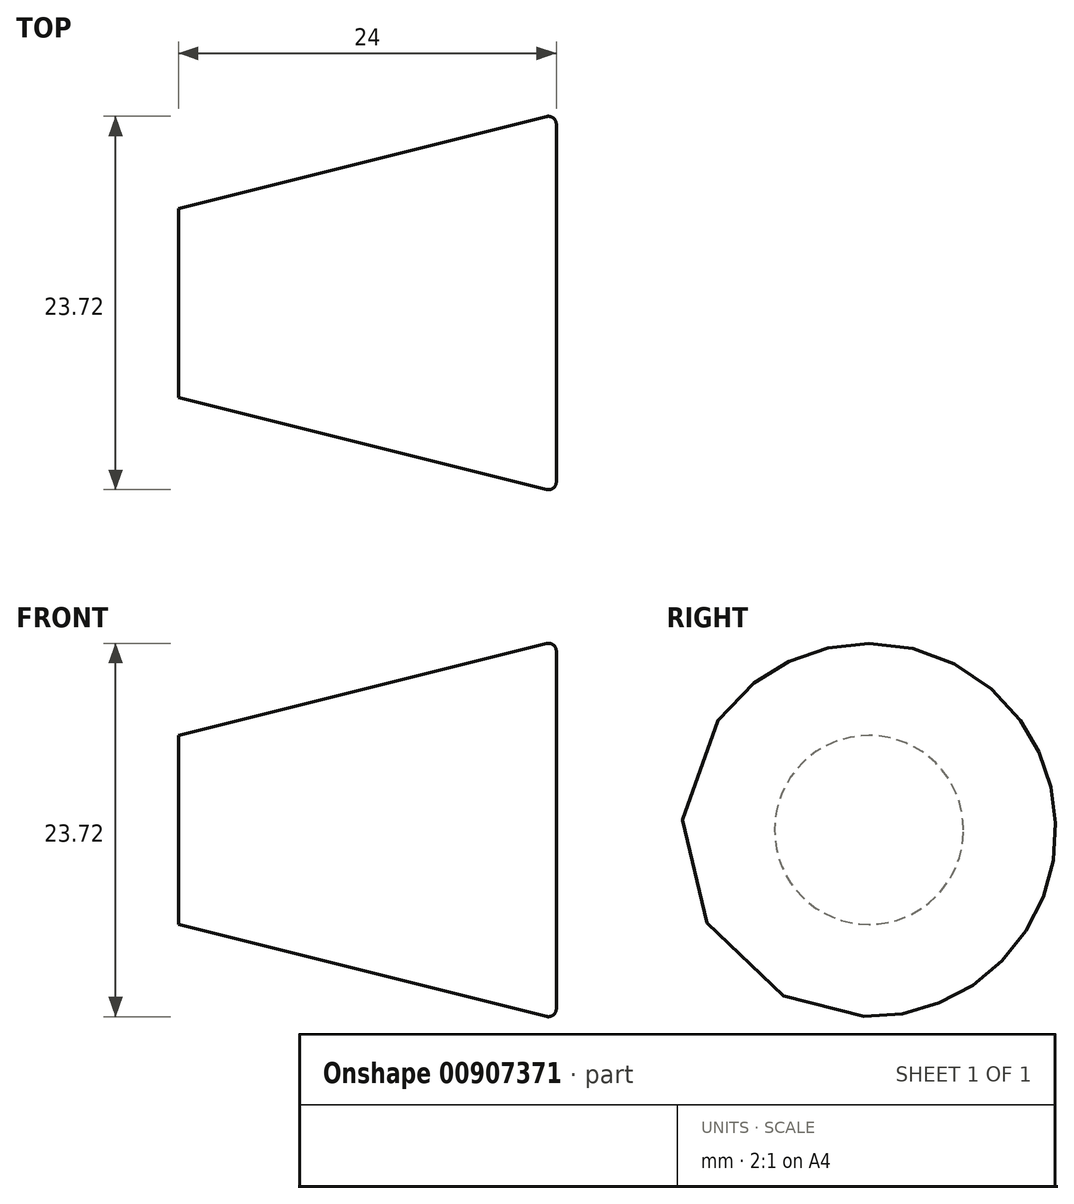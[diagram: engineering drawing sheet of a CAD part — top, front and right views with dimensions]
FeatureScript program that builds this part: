
annotation { "Feature Type Name" : "Feature", "Feature Type Description" : "" }
export const myFeature = defineFeature(function(context is Context, id is Id, definition is map)
    precondition{}
    {
        {
            var Q0;
            Q0=qCreatedBy(makeId("Front.planeOp"),FACE);
            var sketch = newSketch(context, id + "F0", { "sketchPlane" : qUnion([Q0])});
            skLineSegment(sketch, "E0", {"start": v(0, 0) * mm, "end": v(0, 6) * mm});
            skLineSegment(sketch, "E1", {"start": v(0, 6) * mm, "end": v(24, 12) * mm});
            skLineSegment(sketch, "E2", {"start": v(24, 12) * mm, "end": v(24, 0) * mm});
            skLineSegment(sketch, "E3", {"start": v(24, 0) * mm, "end": v(0, 0) * mm});
            skSolve(sketch);
        }
        {
            var Q0;
            Q0 = qSketchRegion(id + "F0", true);
            var Q1;
            Q1=sQuery(id+"F0.wireOp",EDGE,"E3");
            revolve(context, id + "F1", {"surfaceOperationType" : NewSurfaceOperationType.NEW, "entities" : qUnion([Q0]), "axis" : qUnion([Q1]), "revolveType" : RevolveType.FULL});
        }
        {
            var Q0;
            Q0=makeQuery(id+"F1.opRevolve","SWEPT_EDGE",EDGE,{"disambiguationData":[OSD([sQuery(id+"F0.wireOp",EDGE,"E1"),sQuery(id+"F0.wireOp",EDGE,"E2")])]});
            fillet(context, id + "F2", {"entities" : qUnion([Q0]), "tangentPropagation" : true, "radius" : 0.5 * mm, "defaultsChanged" : true, "vertexSettings" : [], "allowEdgeOverflow" : false});
        }
    });
